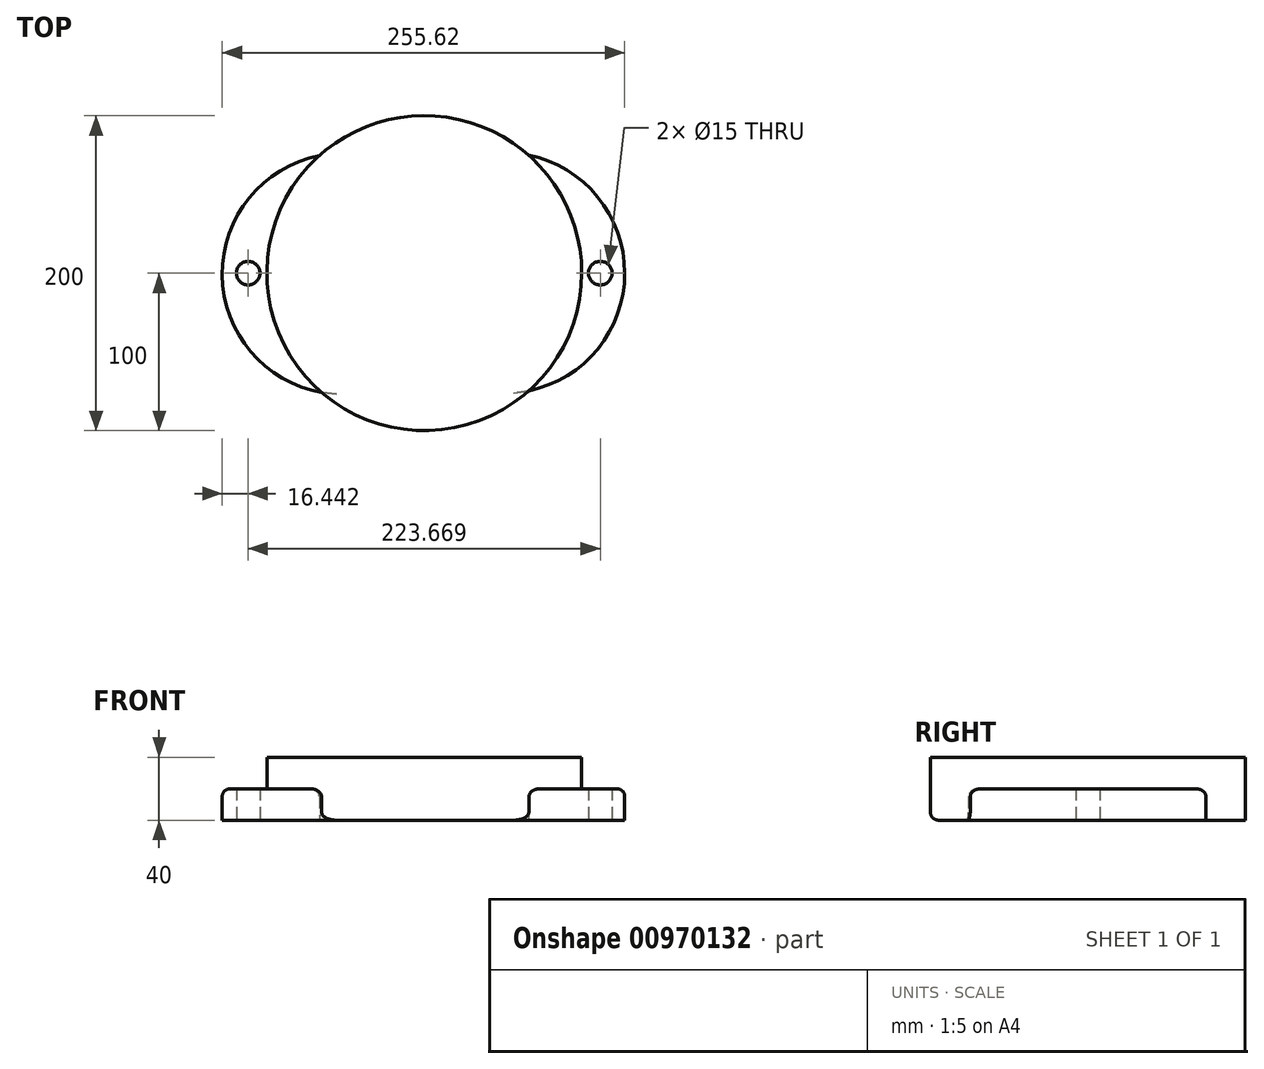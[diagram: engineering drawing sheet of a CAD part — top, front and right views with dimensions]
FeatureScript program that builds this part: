
annotation { "Feature Type Name" : "Feature", "Feature Type Description" : "" }
export const myFeature = defineFeature(function(context is Context, id is Id, definition is map)
    precondition{}
    {
        {
            var Q0;
            Q0=qCreatedBy(makeId("Top.planeOp"),FACE);
            var sketch = newSketch(context, id + "F0", { "sketchPlane" : qUnion([Q0])});
            skCircle(sketch, "E0", {"center": v(0, 0) * mm, "radius": 100 * mm});
            skArc(sketch, "E1", {"start": v(-66.65, 74.55) * mm, "mid": v(-128.32, -1.17) * mm, "end": v(-65.28, -75.76) * mm});
            skArc(sketch, "E2", {"start": v(66.4, -74.77) * mm, "mid": v(127.3, 0.2) * mm, "end": v(66.18, 74.97) * mm});
            skSolve(sketch);
        }
        {
            var Q0;
            {var subQ0=sQuery(id+"F0.wireOp",EDGE,"E1");var subQ1=sQuery(id+"F0.wireOp",EDGE,"E0");var subQ2=makeQuery(id+"F0.imprint","INTERSECT",VERTEX,{"disambiguationData":[OD(0.0)],"derivedFrom":[subQ1,subQ0]});Q0=makeQuery(id+"F0.imprint","IMPRINT",FACE,{"disambiguationData":[TD([[makeQuery(id+"F0.imprint","IMPRINT",EDGE,{"disambiguationData":[TD([[subQ2,1.0]])],"derivedFrom":subQ1}),1.0]])]});}
            extrude(context, id + "F1", {"entities" : qUnion([Q0]), "depth" : 40 * mm, "offsetDistance" : 25 * mm});
        }
        {
            var Q0;
            {var subQ0=sQuery(id+"F0.wireOp",EDGE,"E2");Q0=makeQuery(id+"F0.imprint","IMPRINT",FACE,{"disambiguationData":[TD([[makeQuery(id+"F0.imprint","IMPRINT",EDGE,{"derivedFrom":subQ0}),1.0]])]});}
            var Q1;
            {var subQ0=sQuery(id+"F0.wireOp",EDGE,"E1");Q1=makeQuery(id+"F0.imprint","IMPRINT",FACE,{"disambiguationData":[TD([[makeQuery(id+"F0.imprint","IMPRINT",EDGE,{"derivedFrom":subQ0}),1.0]])]});}
            extrude(context, id + "F2", {"entities" : qUnion([Q0, Q1]), "operationType" : NewBodyOperationType.ADD, "depth" : 20 * mm, "offsetDistance" : 25 * mm});
        }
        {
            var Q0;
            Q0=makeQuery(id+"F2.opExtrude","CAP_EDGE",EDGE,{"disambiguationData":[OSD([sQuery(id+"F0.wireOp",EDGE,"E1")])],"isStart":false});
            var Q1;
            Q1=makeQuery(id+"F2.opExtrude","CAP_EDGE",EDGE,{"disambiguationData":[OSD([sQuery(id+"F0.wireOp",EDGE,"E2")])],"isStart":false});
            var Q2;
            {var subQ0=sQuery(id+"F0.wireOp",EDGE,"E2");var subQ1=sQuery(id+"F0.wireOp",EDGE,"E0");Q2=makeQuery(id+"F2.opExtrude","SWEPT_EDGE",EDGE,{"disambiguationData":[OSD([subQ1,subQ0]),TDD([makeQuery(id+"F0.imprint","INTERSECT",VERTEX,{"disambiguationData":[OD(0.0)],"derivedFrom":[subQ1,subQ0]})])]});}
            var Q3;
            {var subQ0=sQuery(id+"F0.wireOp",EDGE,"E1");var subQ1=sQuery(id+"F0.wireOp",EDGE,"E0");Q3=makeQuery(id+"F2.opExtrude","SWEPT_EDGE",EDGE,{"disambiguationData":[OSD([subQ1,subQ0]),TDD([makeQuery(id+"F0.imprint","INTERSECT",VERTEX,{"disambiguationData":[OD(1.0)],"derivedFrom":[subQ1,subQ0]})])]});}
            var Q4;
            {var subQ0=sQuery(id+"F0.wireOp",EDGE,"E2");var subQ1=sQuery(id+"F0.wireOp",EDGE,"E0");Q4=makeQuery(id+"F2.opExtrude","SWEPT_EDGE",EDGE,{"disambiguationData":[OSD([subQ1,subQ0]),TDD([makeQuery(id+"F0.imprint","INTERSECT",VERTEX,{"disambiguationData":[OD(1.0)],"derivedFrom":[subQ1,subQ0]})])]});}
            var Q5;
            {var subQ0=sQuery(id+"F0.wireOp",EDGE,"E1");var subQ1=sQuery(id+"F0.wireOp",EDGE,"E0");Q5=makeQuery(id+"F2.opExtrude","SWEPT_EDGE",EDGE,{"disambiguationData":[OSD([subQ1,subQ0]),TDD([makeQuery(id+"F0.imprint","INTERSECT",VERTEX,{"disambiguationData":[OD(0.0)],"derivedFrom":[subQ1,subQ0]})])]});}
            fillet(context, id + "F3", {"entities" : qUnion([Q0, Q1, Q2, Q3, Q4, Q5]), "radius" : 5 * mm, "tangentPropagation" : true, "allowEdgeOverflow" : false});
        }
        {
            var Q0;
            Q0=makeQuery(id+"F2.boolean.opBoolean","SPLIT",EDGE,{"disambiguationData":[OD(1.0)],"derivedFrom":makeQuery(id+"F1.opExtrude","CAP_EDGE",EDGE,{"disambiguationData":[OSD([sQuery(id+"F0.wireOp",EDGE,"E0")])],"isStart":true})});
            fillet(context, id + "F4", {"entities" : qUnion([Q0]), "radius" : 5 * mm, "tangentPropagation" : true, "allowEdgeOverflow" : false});
        }
        {
            var Q0;
            {var subQ0=sQuery(id+"F0.wireOp",EDGE,"E1");Q0=makeQuery(id+"F0.imprint","IMPRINT",FACE,{"disambiguationData":[TD([[makeQuery(id+"F0.imprint","IMPRINT",EDGE,{"derivedFrom":subQ0}),1.0]])]});}
            var sketch = newSketch(context, id + "F5", { "sketchPlane" : qUnion([Q0])});
            skCircle(sketch, "E3", {"center": v(-111.88, 0) * mm, "radius": 7.5 * mm});
            skCircle(sketch, "E4", {"center": v(111.8, 0) * mm, "radius": 7.5 * mm});
            skSolve(sketch);
        }
        {
            var Q0;
            Q0=makeQuery(id+"F5.imprint","IMPRINT",FACE,{"disambiguationData":[TD([[makeQuery(id+"F5.imprint","IMPRINT",EDGE,{"derivedFrom":sQuery(id+"F5.wireOp",EDGE,"E3")}),1.0]])]});
            var Q1;
            Q1=makeQuery(id+"F5.imprint","IMPRINT",FACE,{"disambiguationData":[TD([[makeQuery(id+"F5.imprint","IMPRINT",EDGE,{"derivedFrom":sQuery(id+"F5.wireOp",EDGE,"E4")}),1.0]])]});
            extrude(context, id + "F6", {"entities" : qUnion([Q0, Q1]), "operationType" : NewBodyOperationType.REMOVE, "depth" : 87 * mm, "offsetDistance" : 25 * mm});
        }
    });
